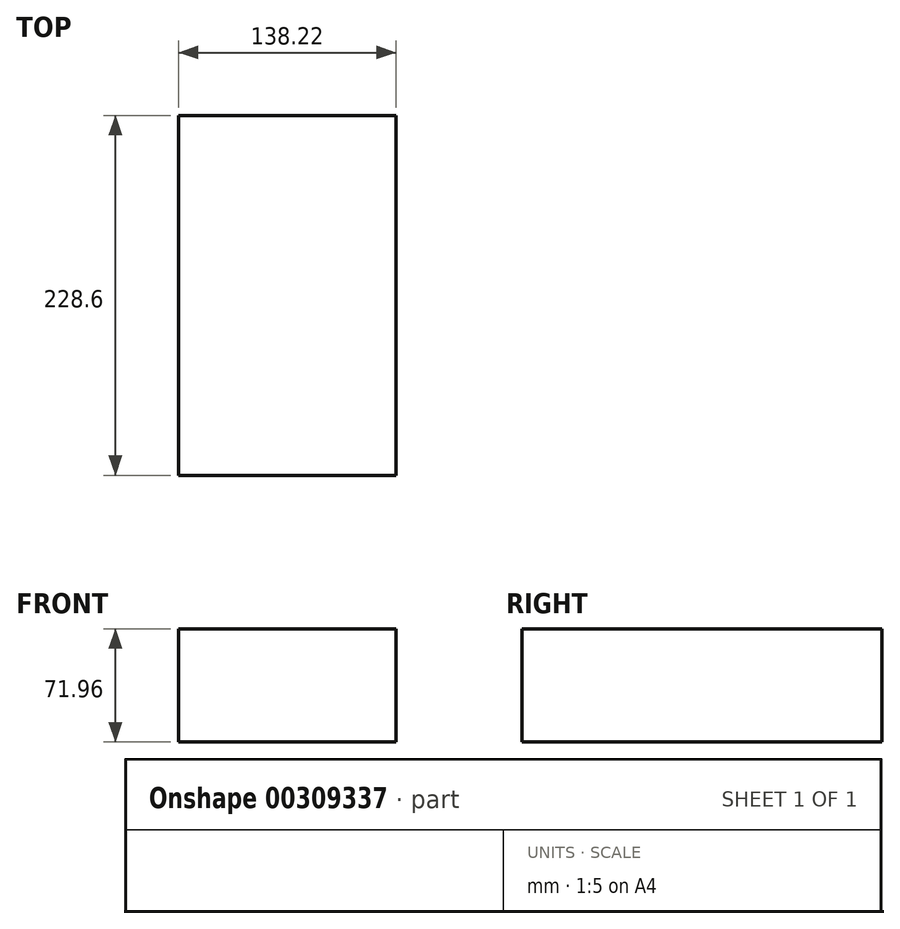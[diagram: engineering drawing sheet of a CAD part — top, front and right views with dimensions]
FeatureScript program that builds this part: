
annotation { "Feature Type Name" : "Feature", "Feature Type Description" : "" }
export const myFeature = defineFeature(function(context is Context, id is Id, definition is map)
    precondition{}
    {
        {
            var Q0;
            Q0=qCreatedBy(makeId("Front.planeOp"),FACE);
            var sketch = newSketch(context, id + "F0", { "sketchPlane" : qUnion([Q0])});
            skLineSegment(sketch, "E0.bottom", {"start": v(-69.1, 35.98) * mm, "end": v(69.1, 35.98) * mm});
            skLineSegment(sketch, "E0.top", {"start": v(-69.1, -35.98) * mm, "end": v(69.1, -35.98) * mm});
            skLineSegment(sketch, "E0.left", {"start": v(-69.1, 35.98) * mm, "end": v(-69.1, -35.98) * mm});
            skLineSegment(sketch, "E0.right", {"start": v(69.1, 35.98) * mm, "end": v(69.1, -35.98) * mm});
            skPoint(sketch, "E0.middle", {"position": v(0, 0) * mm});
            skSolve(sketch);
        }
        {
            var Q0;
            Q0=makeQuery(id+"F0.imprint","IMPRINT",FACE,{"disambiguationData":[TD([[makeQuery(id+"F0.imprint","IMPRINT",EDGE,{"derivedFrom":sQuery(id+"F0.wireOp",EDGE,"E0.bottom")}),-1.0]])]});
            extrude(context, id + "F1", {"entities" : qUnion([Q0]), "endBound" : BoundingType.SYMMETRIC, "depth" : 228.6 * mm});
        }
    });
